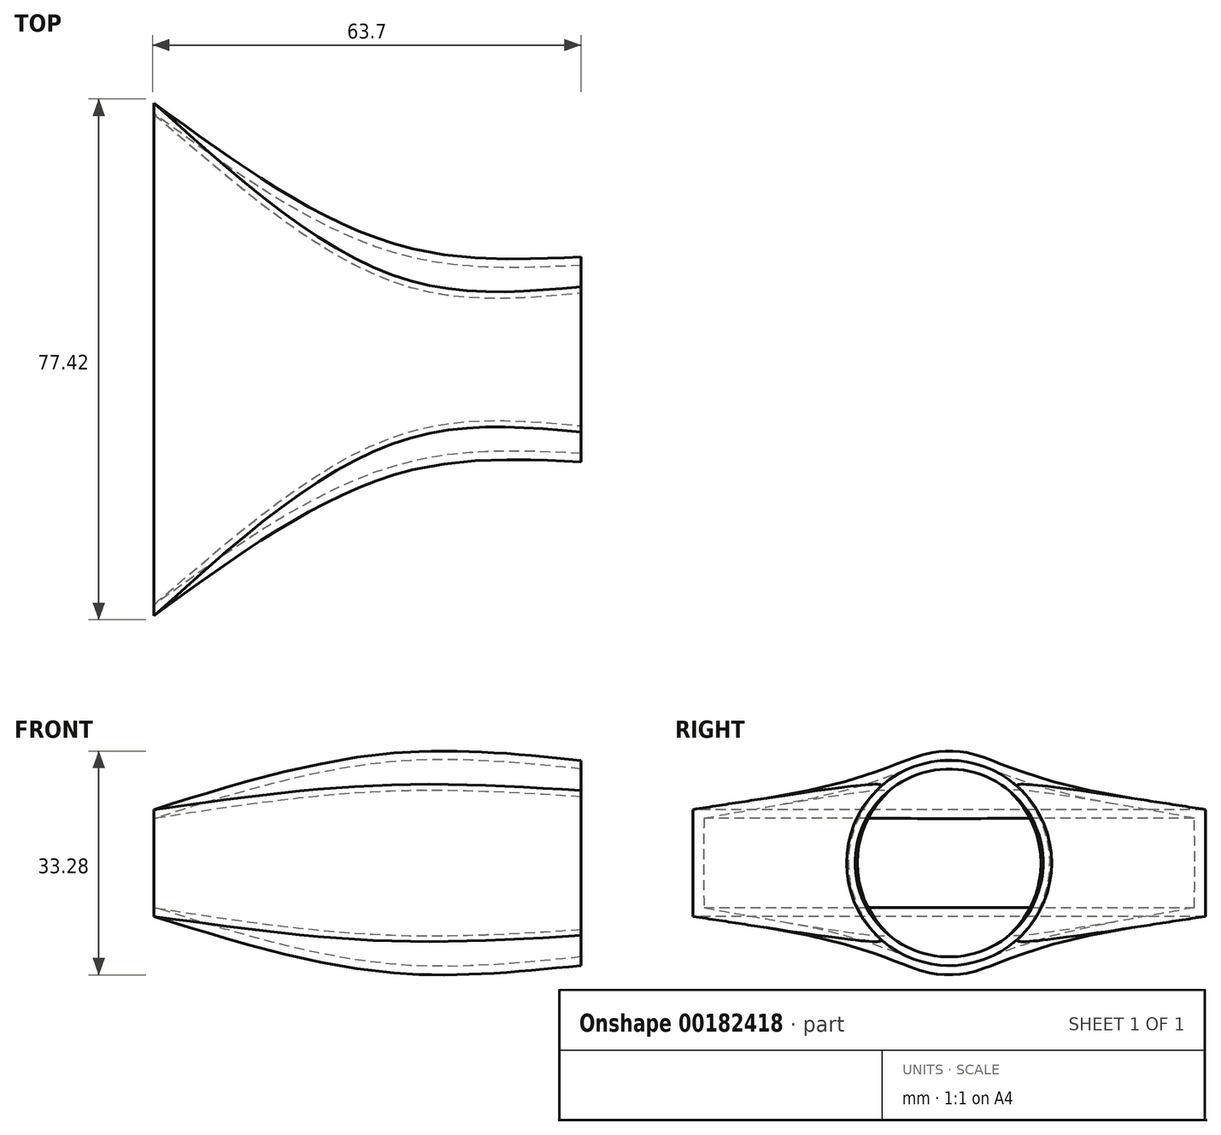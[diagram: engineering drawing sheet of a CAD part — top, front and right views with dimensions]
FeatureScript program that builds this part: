
annotation { "Feature Type Name" : "Feature", "Feature Type Description" : "" }
export const myFeature = defineFeature(function(context is Context, id is Id, definition is map)
    precondition{}
    {
        {
            var Q0;
            Q0=qCreatedBy(makeId("Right.planeOp"),FACE);
            var sketch = newSketch(context, id + "F0", { "sketchPlane" : qUnion([Q0])});
            skLineSegment(sketch, "E0.bottom", {"start": v(38.1, -7.94) * mm, "end": v(-38.1, -7.94) * mm});
            skLineSegment(sketch, "E0.top", {"start": v(38.1, 7.94) * mm, "end": v(-38.1, 7.94) * mm});
            skLineSegment(sketch, "E0.left", {"start": v(38.1, -7.94) * mm, "end": v(38.1, 7.94) * mm});
            skLineSegment(sketch, "E0.right", {"start": v(-38.1, -7.94) * mm, "end": v(-38.1, 7.94) * mm});
            skPoint(sketch, "E0.middle", {"position": v(0, 0) * mm});
            skSolve(sketch);
        }
        {
            var Q0;
            Q0=qCreatedBy(makeId("Right.planeOp"),FACE);
            cPlane(context, id + "F1", {"entities" : qUnion([Q0]), "cplaneType" : CPlaneType.OFFSET, "offset" : 63.5 * mm, "width" : 152.4 * mm, "height" : 152.4 * mm});
        }
        {
            var Q0;
            Q0=qCreatedBy(makeId("Right.planeOp"),FACE);
            cPlane(context, id + "F2", {"entities" : qUnion([Q0]), "cplaneType" : CPlaneType.OFFSET, "offset" : 38.1 * mm, "width" : 152.4 * mm, "height" : 152.4 * mm});
        }
        {
            var Q0;
            Q0=qCreatedBy(id+"F2.planeOp",FACE);
            var sketch = newSketch(context, id + "F3", { "sketchPlane" : qUnion([Q0])});
            skLineSegment(sketch, "E1", {"start": v(0, 0) * mm, "end": v(-13.64, 13.64) * mm, "construction": true});
            skLineSegment(sketch, "E2", {"start": v(0, 0) * mm, "end": v(14.13, 14.13) * mm, "construction": true});
            skLineSegment(sketch, "E3.MirrorCS", {"start": v(0, 0) * mm, "end": v(-11.67, -11.67) * mm, "construction": true});
            skLineSegment(sketch, "E4.MirrorCS", {"start": v(0, 0) * mm, "end": v(14.13, -14.13) * mm, "construction": true});
            skArc(sketch, "E5", {"start": v(-11.67, 11.67) * mm, "mid": v(-11.67, -11.67) * mm, "end": v(11.67, -11.67) * mm});
            skArc(sketch, "E6", {"start": v(11.67, 11.67) * mm, "mid": v(0, 16.51) * mm, "end": v(-11.67, 11.67) * mm});
            skArc(sketch, "E7", {"start": v(11.67, -11.67) * mm, "mid": v(16.51, 0) * mm, "end": v(11.67, 11.67) * mm});
            skLineSegment(sketch, "E8", {"start": v(-11.67, -11.67) * mm, "end": v(-13.64, -13.64) * mm, "construction": true});
            skSolve(sketch);
        }
        {
            var Q0;
            Q0=qCreatedBy(id+"F1.planeOp",FACE);
            var sketch = newSketch(context, id + "F4", { "sketchPlane" : qUnion([Q0])});
            skCircle(sketch, "E9", {"center": v(0, 0) * mm, "radius": 15.24 * mm});
            skLineSegment(sketch, "E10.0", {"start": v(0, 0) * mm, "end": v(-10.78, 10.78) * mm, "construction": true});
            skLineSegment(sketch, "E11.0", {"start": v(0, 0) * mm, "end": v(14.13, 14.13) * mm, "construction": true});
            skLineSegment(sketch, "E12.0", {"start": v(0, 0) * mm, "end": v(-11.67, -11.67) * mm, "construction": true});
            skLineSegment(sketch, "E13.0", {"start": v(0, 0) * mm, "end": v(14.13, -14.13) * mm, "construction": true});
            skLineSegment(sketch, "E14", {"start": v(-10.78, 10.78) * mm, "end": v(-13.64, 13.64) * mm, "construction": true});
            skSolve(sketch);
        }
        {
            var Q0;
            Q0=makeQuery(id+"F0.imprint","IMPRINT",FACE,{"disambiguationData":[TD([[makeQuery(id+"F0.imprint","IMPRINT",EDGE,{"derivedFrom":sQuery(id+"F0.wireOp",EDGE,"E0.bottom")}),-1.0]])]});
            var Q1;
            Q1=makeQuery(id+"F3.imprint","IMPRINT",FACE,{"disambiguationData":[TD([[makeQuery(id+"F3.imprint","IMPRINT",EDGE,{"derivedFrom":sQuery(id+"F3.wireOp",EDGE,"E5")}),1.0]])]});
            var Q2;
            Q2=makeQuery(id+"F4.imprint","IMPRINT",FACE,{"disambiguationData":[TD([[makeQuery(id+"F4.imprint","IMPRINT",EDGE,{"derivedFrom":sQuery(id+"F4.wireOp",EDGE,"E9")}),1.0]])]});
            var Q3;
            Q3=makeQuery(id+"F0.imprint","IMPRINT",FACE,{"disambiguationData":[TD([[makeQuery(id+"F0.imprint","IMPRINT",EDGE,{"derivedFrom":sQuery(id+"F0.wireOp",EDGE,"E0.bottom")}),-1.0]])]});
            var Q4;
            Q4=makeQuery(id+"F3.imprint","IMPRINT",FACE,{"disambiguationData":[TD([[makeQuery(id+"F3.imprint","IMPRINT",EDGE,{"derivedFrom":sQuery(id+"F3.wireOp",EDGE,"E5")}),1.0]])]});
            var Q5;
            Q5=makeQuery(id+"F4.imprint","IMPRINT",FACE,{"disambiguationData":[TD([[makeQuery(id+"F4.imprint","IMPRINT",EDGE,{"derivedFrom":sQuery(id+"F4.wireOp",EDGE,"E9")}),1.0]])]});
            var Q6;
            Q6=sQuery(id+"F3.wireOp",VERTEX,"E6.end");
            var Q7;
            Q7=sQuery(id+"F0.wireOp",VERTEX,"E0.right.end");
            var Q8;
            Q8=sQuery(id+"F4.wireOp",VERTEX,"E14.start");
            loft(context, id + "F5", {"sheetProfilesArray" : [{ "sheetProfileEntities" : qUnion([Q0]) }, { "sheetProfileEntities" : qUnion([Q1]) }, { "sheetProfileEntities" : qUnion([Q2]) }], "wireProfilesArray" : [{ "wireProfileEntities" : qUnion([Q3]) }, { "wireProfileEntities" : qUnion([Q4]) }, { "wireProfileEntities" : qUnion([Q5]) }], "matchConnections" : true, "connections" : [{ "connectionEntities" : qUnion([Q6, Q7, Q8]), "connectionEdgeQueries" : qUnion([]), "connectionEdgeParameters" : [] }]});
        }
        {
            var Q0;
            Q0=makeQuery(id+"F5.opLoft","CAP_FACE",FACE,{"disambiguationData":[OSD([makeQuery(id+"F0.imprint","IMPRINT",FACE,{"disambiguationData":[TD([[makeQuery(id+"F0.imprint","IMPRINT",EDGE,{"derivedFrom":sQuery(id+"F0.wireOp",EDGE,"E0.bottom")}),-1.0]])]})])],"isStart":true});
            var Q1;
            Q1=makeQuery(id+"F5.opLoft","CAP_FACE",FACE,{"disambiguationData":[OSD([makeQuery(id+"F4.imprint","IMPRINT",FACE,{"disambiguationData":[TD([[makeQuery(id+"F4.imprint","IMPRINT",EDGE,{"derivedFrom":sQuery(id+"F4.wireOp",EDGE,"E9")}),1.0]])]})])],"isStart":true});
            shell(context, id + "F6", {"entities" : qUnion([Q0, Q1]), "thickness" : 1.27 * mm});
        }
    });
